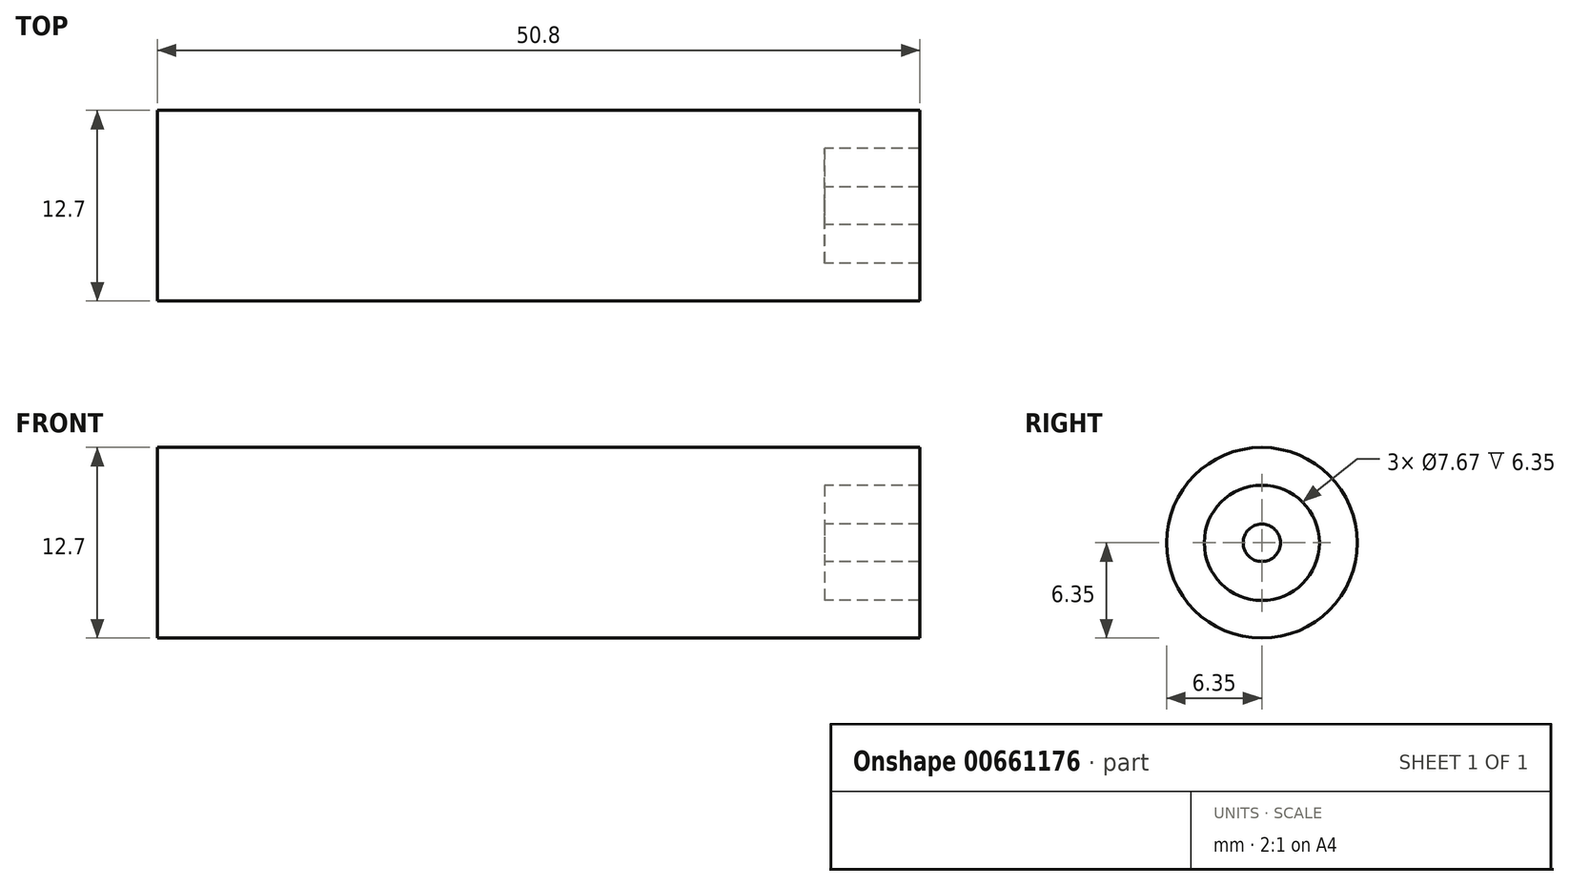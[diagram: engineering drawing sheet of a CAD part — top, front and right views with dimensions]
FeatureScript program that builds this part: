
annotation { "Feature Type Name" : "Feature", "Feature Type Description" : "" }
export const myFeature = defineFeature(function(context is Context, id is Id, definition is map)
    precondition{}
    {
        {
            var Q0;
            Q0=qCreatedBy(makeId("Front.planeOp"),FACE);
            var sketch = newSketch(context, id + "F0", { "sketchPlane" : qUnion([Q0])});
            skLineSegment(sketch, "E0.top", {"start": v(0, 12.7) * mm, "end": v(50.8, 12.7) * mm});
            skLineSegment(sketch, "E0.left", {"start": v(0, 6.35) * mm, "end": v(0, 12.7) * mm});
            skPoint(sketch, "E1", {"position": v(44.45, 10.19) * mm});
            skLineSegment(sketch, "E2", {"start": v(41.91, 6.35) * mm, "end": v(41.91, 12.7) * mm});
            skLineSegment(sketch, "E3", {"start": v(39.37, 6.35) * mm, "end": v(39.37, 12.7) * mm});
            skLineSegment(sketch, "E4.bottom", {"start": v(39.37, 12.7) * mm, "end": v(41.91, 12.7) * mm});
            skLineSegment(sketch, "E4.top", {"start": v(39.37, 15.24) * mm, "end": v(41.91, 15.24) * mm});
            skLineSegment(sketch, "E4.left", {"start": v(39.37, 12.7) * mm, "end": v(39.37, 15.24) * mm});
            skLineSegment(sketch, "E4.right", {"start": v(41.91, 12.7) * mm, "end": v(41.91, 15.24) * mm});
            skLineSegment(sketch, "E5", {"start": v(39.37, 6.35) * mm, "end": v(50.8, 6.35) * mm});
            skPoint(sketch, "E6.orphan", {"position": v(0, 0) * mm});
            skLineSegment(sketch, "E7.trimOffspring", {"start": v(44.45, 6.35) * mm, "end": v(44.45, 12.7) * mm});
            skLineSegment(sketch, "E8.trimOffspring", {"start": v(50.8, 6.35) * mm, "end": v(50.8, 12.7) * mm});
            skLineSegment(sketch, "E9", {"start": v(0, 6.35) * mm, "end": v(39.37, 6.35) * mm});
            skPoint(sketch, "E10", {"position": v(44.45, 7.6) * mm});
            skLineSegment(sketch, "E11", {"start": v(44.45, 10.19) * mm, "end": v(50.8, 10.19) * mm});
            skLineSegment(sketch, "E12", {"start": v(44.45, 7.6) * mm, "end": v(50.8, 7.6) * mm});
            skSolve(sketch);
        }
        {
            var Q0;
            {var subQ0=sQuery(id+"F0.wireOp",EDGE,"pMb3HIgy-95nh-aJB9-dsB2-SHtEXql1WHdN");Q0=makeQuery(id+"F0.imprint","IMPRINT",FACE,{"disambiguationData":[TD([[makeQuery(id+"F0.imprint","IMPRINT",EDGE,{"derivedFrom":subQ0}),-1.0]])]});}
            var Q1;
            {var subQ4=sQuery(id+"F0.wireOp",EDGE,"E2");Q1=makeQuery(id+"F0.imprint","IMPRINT",FACE,{"disambiguationData":[TD([[makeQuery(id+"F0.imprint","IMPRINT",EDGE,{"derivedFrom":subQ4}),-1.0]])]});}
            var Q2;
            {var subQ0=sQuery(id+"F0.wireOp",EDGE,"E2");Q2=makeQuery(id+"F0.imprint","IMPRINT",FACE,{"disambiguationData":[TD([[makeQuery(id+"F0.imprint","IMPRINT",EDGE,{"derivedFrom":subQ0}),1.0]])]});}
            var Q3;
            Q3=makeQuery(id+"F0.imprint","IMPRINT",FACE,{"disambiguationData":[TD([[makeQuery(id+"F0.imprint","IMPRINT",EDGE,{"derivedFrom":sQuery(id+"F0.wireOp",EDGE,"E4.bottom")}),1.0]])]});
            var Q4;
            {var subQ0=sQuery(id+"F0.wireOp",EDGE,"E0.left");Q4=makeQuery(id+"F0.imprint","IMPRINT",FACE,{"disambiguationData":[TD([[makeQuery(id+"F0.imprint","IMPRINT",EDGE,{"derivedFrom":subQ0}),-1.0]])]});}
            var Q5;
            {var subQ5=sQuery(id+"F0.wireOp",EDGE,"Huq6eiVT-hGzC-q7GI-W85S-Tbwof0Tj0cwv");Q5=makeQuery(id+"F0.imprint","IMPRINT",FACE,{"disambiguationData":[TD([[makeQuery(id+"F0.imprint","IMPRINT",EDGE,{"derivedFrom":subQ5}),1.0]])]});}
            var Q6;
            {var subQ5=sQuery(id+"F0.wireOp",EDGE,"E11");Q6=makeQuery(id+"F0.imprint","IMPRINT",FACE,{"disambiguationData":[TD([[makeQuery(id+"F0.imprint","IMPRINT",EDGE,{"derivedFrom":subQ5}),1.0]])]});}
            var Q7;
            {var subQ5=sQuery(id+"F0.wireOp",EDGE,"E12");Q7=makeQuery(id+"F0.imprint","IMPRINT",FACE,{"disambiguationData":[TD([[makeQuery(id+"F0.imprint","IMPRINT",EDGE,{"derivedFrom":subQ5}),-1.0]])]});}
            var Q8;
            Q8=sQuery(id+"F0.wireOp",EDGE,"E9");
            revolve(context, id + "F1", {"entities" : qUnion([Q0, Q1, Q2, Q3, Q4, Q5, Q6, Q7]), "axis" : qUnion([Q8]), "revolveType" : RevolveType.FULL});
        }
    });
